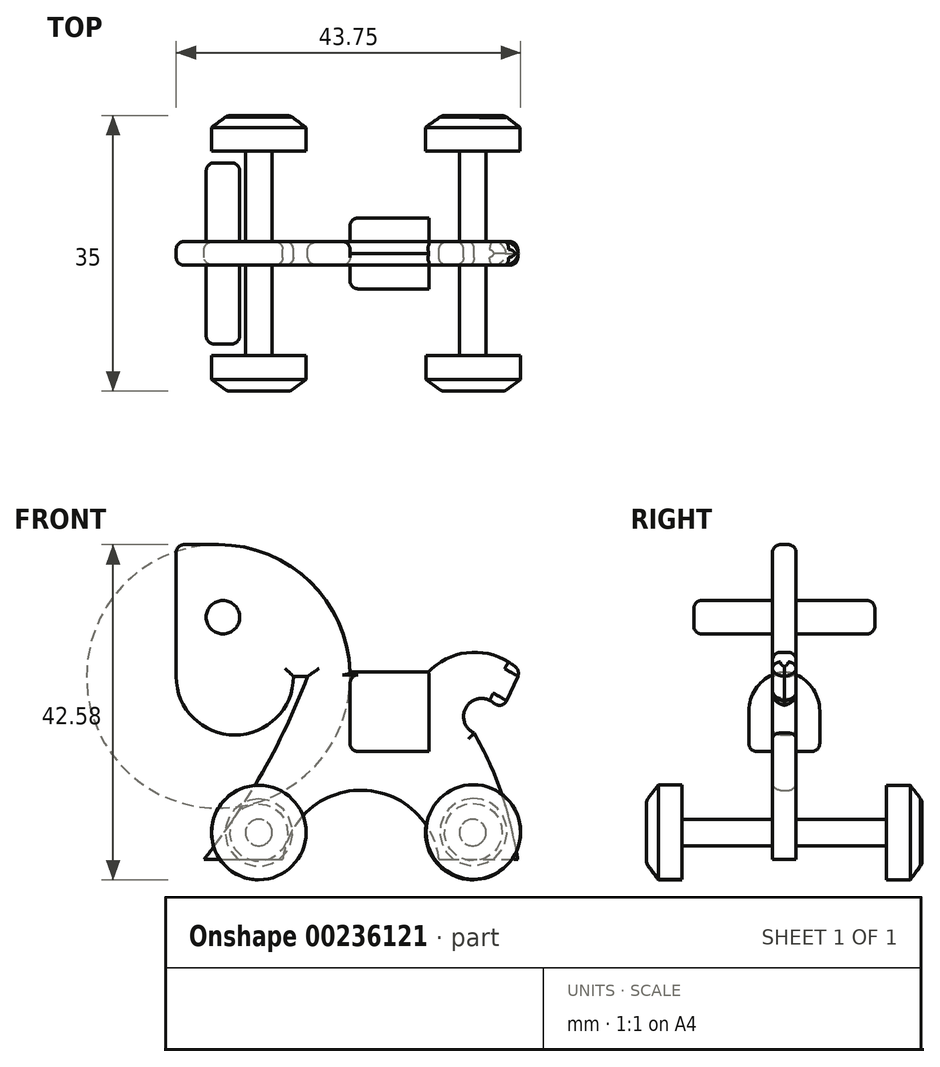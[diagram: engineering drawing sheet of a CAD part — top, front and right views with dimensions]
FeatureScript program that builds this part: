
annotation { "Feature Type Name" : "Feature", "Feature Type Description" : "" }
export const myFeature = defineFeature(function(context is Context, id is Id, definition is map)
    precondition{}
    {
        {
            var Q0;
            Q0=qCreatedBy(makeId("Front.planeOp"),FACE);
            var sketch = newSketch(context, id + "F0", { "sketchPlane" : qUnion([Q0])});
            skLineSegment(sketch, "E0", {"start": v(-55.34, 56.43) * mm, "end": v(-49.98, 56.43) * mm});
            skArc(sketch, "E1", {"start": v(-33.25, 40.31) * mm, "mid": v(-38.36, 51.75) * mm, "end": v(-49.98, 56.43) * mm});
            skLineSegment(sketch, "E2", {"start": v(-33.25, 40.31) * mm, "end": v(-23.25, 40.31) * mm});
            skArc(sketch, "E3", {"start": v(-11.59, 40.31) * mm, "mid": v(-17.42, 42.76) * mm, "end": v(-23.25, 40.31) * mm});
            skLineSegment(sketch, "E4", {"start": v(-55.34, 56.43) * mm, "end": v(-55.34, 39.7) * mm});
            skArc(sketch, "E5", {"start": v(-55.34, 39.7) * mm, "mid": v(-47.9, 32.24) * mm, "end": v(-40.44, 39.7) * mm});
            skLineSegment(sketch, "E6", {"start": v(-40.44, 39.7) * mm, "end": v(-38.64, 39.7) * mm});
            skArc(sketch, "E7", {"start": v(-51.8, 16.43) * mm, "mid": v(-44.34, 27.56) * mm, "end": v(-38.64, 39.7) * mm});
            skLineSegment(sketch, "E8", {"start": v(-51.8, 16.43) * mm, "end": v(-41.8, 16.43) * mm});
            skArc(sketch, "E9", {"start": v(-21.94, 16.43) * mm, "mid": v(-31.87, 25.23) * mm, "end": v(-41.8, 16.43) * mm});
            skArc(sketch, "E10", {"start": v(-14.24, 34.6) * mm, "mid": v(-17.77, 36.53) * mm, "end": v(-17.48, 32.51) * mm});
            skLineSegment(sketch, "E11", {"start": v(-14.24, 34.6) * mm, "end": v(-11.59, 40.31) * mm});
            skArc(sketch, "E12", {"start": v(-11.94, 16.43) * mm, "mid": v(-13.97, 24.73) * mm, "end": v(-17.48, 32.51) * mm});
            skLineSegment(sketch, "E13", {"start": v(-21.94, 16.43) * mm, "end": v(-11.94, 16.43) * mm});
            skCircle(sketch, "E14", {"center": v(-49.4, 47.21) * mm, "radius": 2.13 * mm});
            skCircle(sketch, "E15", {"center": v(-44.84, 19.85) * mm, "radius": 1.7 * mm});
            skCircle(sketch, "E16", {"center": v(-17.67, 19.85) * mm, "radius": 1.7 * mm});
            skSolve(sketch);
        }
        {
            var Q0;
            Q0=qSketchRegion(id+"F0",true);
            extrude(context, id + "F1", {"entities" : qUnion([Q0]), "depth" : 3 * mm});
        }
        {
            var Q0;
            Q0=makeQuery(id+"F1.opExtrude","CAP_FACE",FACE,{"disambiguationData":[OSD([sQuery(id+"F0.wireOp",EDGE,"E0"),sQuery(id+"F0.wireOp",EDGE,"E1"),sQuery(id+"F0.wireOp",EDGE,"E2"),sQuery(id+"F0.wireOp",EDGE,"E3"),sQuery(id+"F0.wireOp",EDGE,"E4"),sQuery(id+"F0.wireOp",EDGE,"E5"),sQuery(id+"F0.wireOp",EDGE,"E6"),sQuery(id+"F0.wireOp",EDGE,"E7"),sQuery(id+"F0.wireOp",EDGE,"E8"),sQuery(id+"F0.wireOp",EDGE,"E9"),sQuery(id+"F0.wireOp",EDGE,"E10"),sQuery(id+"F0.wireOp",EDGE,"E11"),sQuery(id+"F0.wireOp",EDGE,"E12"),sQuery(id+"F0.wireOp",EDGE,"E13"),sQuery(id+"F0.wireOp",EDGE,"E14"),sQuery(id+"F0.wireOp",EDGE,"E15"),sQuery(id+"F0.wireOp",EDGE,"E16")])],"isStart":false});
            var sketch = newSketch(context, id + "F2", { "sketchPlane" : qUnion([Q0])});
            skSolve(sketch);
        }
        {
            var Q0;
            Q0=makeQuery(id+"F2.imprint","IMPRINT",FACE,{"disambiguationData":[TD([[makeQuery(id+"F2.imprint","IMPRINT",EDGE,{"derivedFrom":makeQuery(id+"F1.opExtrude","CAP_EDGE",EDGE,{"disambiguationData":[OSD([sQuery(id+"F0.wireOp",EDGE,"E15")])],"isStart":false})}),1.0]])]});
            var Q1;
            Q1=makeQuery(id+"F2.imprint","IMPRINT",FACE,{"disambiguationData":[TD([[makeQuery(id+"F2.imprint","IMPRINT",EDGE,{"derivedFrom":makeQuery(id+"F1.opExtrude","CAP_EDGE",EDGE,{"disambiguationData":[OSD([sQuery(id+"F0.wireOp",EDGE,"E16")])],"isStart":false})}),1.0]])]});
            extrude(context, id + "F3", {"entities" : qUnion([Q0, Q1]), "operationType" : NewBodyOperationType.ADD, "depth" : 13 * mm, "hasSecondDirection" : true, "secondDirectionOppositeDirection" : true, "secondDirectionDepth" : 16 * mm});
        }
        {
            var Q0;
            Q0=makeQuery(id+"F3.opExtrude","CAP_FACE",FACE,{"disambiguationData":[OSD([sQuery(id+"F0.wireOp",EDGE,"E15")])],"isStart":false});
            var sketch = newSketch(context, id + "F4", { "sketchPlane" : qUnion([Q0])});
            skCircle(sketch, "E17", {"center": v(-44.84, 19.85) * mm, "radius": 6 * mm});
            skCircle(sketch, "E18", {"center": v(-17.59, 19.94) * mm, "radius": 6 * mm});
            skSolve(sketch);
        }
        {
            var Q0;
            Q0=makeQuery(id+"F4.imprint","IMPRINT",FACE,{"disambiguationData":[TD([[makeQuery(id+"F4.imprint","IMPRINT",EDGE,{"derivedFrom":sQuery(id+"F4.wireOp",EDGE,"E18")}),1.0]])]});
            var Q1;
            Q1=makeQuery(id+"F4.imprint","IMPRINT",FACE,{"disambiguationData":[TD([[makeQuery(id+"F4.imprint","IMPRINT",EDGE,{"derivedFrom":sQuery(id+"F4.wireOp",EDGE,"E17")}),1.0]])]});
            var Q2;
            Q2=makeQuery(id+"F4.imprint","IMPRINT",FACE,{"disambiguationData":[TD([[makeQuery(id+"F4.imprint","IMPRINT",EDGE,{"derivedFrom":makeQuery(id+"F3.opExtrude","CAP_EDGE",EDGE,{"disambiguationData":[OSD([sQuery(id+"F0.wireOp",EDGE,"E15")])],"isStart":false})}),1.0]])]});
            extrude(context, id + "F5", {"entities" : qUnion([Q0, Q1, Q2]), "operationType" : NewBodyOperationType.ADD, "endBound" : BoundingType.SYMMETRIC, "oppositeDirection" : true, "depth" : 3 * mm});
        }
        {
            var Q0;
            Q0=makeQuery(id+"F3.opExtrude","CAP_FACE",FACE,{"disambiguationData":[OSD([sQuery(id+"F0.wireOp",EDGE,"E16")])],"isStart":true});
            var sketch = newSketch(context, id + "F6", { "sketchPlane" : qUnion([Q0])});
            skCircle(sketch, "E19", {"center": v(44.85, 19.85) * mm, "radius": 6 * mm});
            skCircle(sketch, "E20", {"center": v(17.67, 19.85) * mm, "radius": 6 * mm});
            skCircle(sketch, "E21", {"center": v(44.85, 19.85) * mm, "radius": 6.02 * mm});
            skSolve(sketch);
        }
        {
            var Q0;
            Q0=makeQuery(id+"F6.imprint","IMPRINT",FACE,{"disambiguationData":[TD([[makeQuery(id+"F6.imprint","IMPRINT",EDGE,{"derivedFrom":sQuery(id+"F6.wireOp",EDGE,"E20")}),1.0]])]});
            var Q1;
            Q1=makeQuery(id+"F6.imprint","IMPRINT",FACE,{"disambiguationData":[TD([[makeQuery(id+"F6.imprint","IMPRINT",EDGE,{"derivedFrom":sQuery(id+"F6.wireOp",EDGE,"E19")}),1.0]])]});
            var Q2;
            Q2=makeQuery(id+"F6.imprint","IMPRINT",FACE,{"disambiguationData":[TD([[makeQuery(id+"F6.imprint","IMPRINT",EDGE,{"derivedFrom":makeQuery(id+"F3.opExtrude","CAP_EDGE",EDGE,{"disambiguationData":[OSD([sQuery(id+"F0.wireOp",EDGE,"E16")])],"isStart":true})}),-1.0]])]});
            extrude(context, id + "F7", {"entities" : qUnion([Q0, Q1, Q2]), "operationType" : NewBodyOperationType.ADD, "endBound" : BoundingType.SYMMETRIC, "oppositeDirection" : true, "depth" : 3 * mm});
        }
        {
            var Q0;
            Q0=makeQuery(id+"F1.opExtrude","CAP_FACE",FACE,{"disambiguationData":[OSD([sQuery(id+"F0.wireOp",EDGE,"E0"),sQuery(id+"F0.wireOp",EDGE,"E1"),sQuery(id+"F0.wireOp",EDGE,"E2"),sQuery(id+"F0.wireOp",EDGE,"E3"),sQuery(id+"F0.wireOp",EDGE,"E4"),sQuery(id+"F0.wireOp",EDGE,"E5"),sQuery(id+"F0.wireOp",EDGE,"E6"),sQuery(id+"F0.wireOp",EDGE,"E7"),sQuery(id+"F0.wireOp",EDGE,"E8"),sQuery(id+"F0.wireOp",EDGE,"E9"),sQuery(id+"F0.wireOp",EDGE,"E10"),sQuery(id+"F0.wireOp",EDGE,"E11"),sQuery(id+"F0.wireOp",EDGE,"E12"),sQuery(id+"F0.wireOp",EDGE,"E13"),sQuery(id+"F0.wireOp",EDGE,"E14"),sQuery(id+"F0.wireOp",EDGE,"E15"),sQuery(id+"F0.wireOp",EDGE,"E16")])],"isStart":true});
            var sketch = newSketch(context, id + "F8", { "sketchPlane" : qUnion([Q0])});
            skLineSegment(sketch, "E22", {"start": v(23.25, 40.31) * mm, "end": v(23.25, 30.15) * mm});
            skLineSegment(sketch, "E23", {"start": v(23.25, 30.15) * mm, "end": v(33.25, 30.15) * mm});
            skLineSegment(sketch, "E24", {"start": v(33.25, 30.15) * mm, "end": v(33.25, 40.31) * mm});
            skLineSegment(sketch, "E25", {"start": v(33.25, 40.31) * mm, "end": v(23.25, 40.31) * mm});
            skSolve(sketch);
        }
        {
            var Q0;
            Q0=makeQuery(id+"F8.imprint","IMPRINT",FACE,{"disambiguationData":[TD([[makeQuery(id+"F8.imprint","IMPRINT",EDGE,{"derivedFrom":sQuery(id+"F8.wireOp",EDGE,"E22")}),1.0]])]});
            extrude(context, id + "F9", {"entities" : qUnion([Q0]), "operationType" : NewBodyOperationType.ADD, "depth" : 3 * mm, "hasSecondDirection" : true, "secondDirectionOppositeDirection" : true, "secondDirectionDepth" : 6 * mm});
        }
        {
            var Q0;
            Q0=makeQuery(id+"F9.opExtrude","CAP_EDGE",EDGE,{"disambiguationData":[OSD([sQuery(id+"F8.wireOp",EDGE,"E25")])],"isStart":false});
            var Q1;
            Q1=makeQuery(id+"F9.opExtrude","CAP_EDGE",EDGE,{"disambiguationData":[OSD([sQuery(id+"F8.wireOp",EDGE,"E25")])],"isStart":true});
            fillet(context, id + "F10", {"entities" : qUnion([Q0, Q1]), "radius" : 5 * mm, "tangentPropagation" : true, "allowEdgeOverflow" : false});
        }
        {
            var Q0;
            Q0=makeQuery(id+"F8.imprint","IMPRINT",FACE,{"disambiguationData":[TD([[makeQuery(id+"F8.imprint","IMPRINT",EDGE,{"derivedFrom":makeQuery(id+"F1.opExtrude","CAP_EDGE",EDGE,{"disambiguationData":[OSD([sQuery(id+"F0.wireOp",EDGE,"E14")])],"isStart":true})}),-1.0]])]});
            extrude(context, id + "F11", {"entities" : qUnion([Q0]), "operationType" : NewBodyOperationType.ADD, "depth" : 10 * mm, "hasSecondDirection" : true, "secondDirectionOppositeDirection" : true, "secondDirectionDepth" : 13 * mm});
        }
        {
            var Q0;
            Q0=makeQuery(id+"F4.imprint","IMPRINT",FACE,{"disambiguationData":[TD([[makeQuery(id+"F4.imprint","IMPRINT",EDGE,{"derivedFrom":sQuery(id+"F4.wireOp",EDGE,"E17")}),1.0]])]});
            var Q1;
            Q1=makeQuery(id+"F4.imprint","IMPRINT",FACE,{"disambiguationData":[TD([[makeQuery(id+"F4.imprint","IMPRINT",EDGE,{"derivedFrom":sQuery(id+"F4.wireOp",EDGE,"E18")}),1.0]])]});
            cPlane(context, id + "F12", {"entities" : qUnion([Q0, Q1]), "cplaneType" : CPlaneType.MID_PLANE, "offset" : 25 * mm, "width" : 150 * mm, "height" : 150 * mm});
        }
        {
            var Q0;
            Q0=qCreatedBy(id+"F12.planeOp",FACE);
            cPlane(context, id + "F13", {"entities" : qUnion([Q0]), "cplaneType" : CPlaneType.OFFSET, "offset" : 3 * mm, "width" : 150 * mm, "height" : 150 * mm});
        }
        {
            var Q0;
            Q0=qCreatedBy(id+"F13.planeOp",FACE);
            var sketch = newSketch(context, id + "F14", { "sketchPlane" : qUnion([Q0])});
            skCircle(sketch, "E26", {"center": v(-44.84, 19.85) * mm, "radius": 4 * mm});
            skCircle(sketch, "E27", {"center": v(-17.59, 19.94) * mm, "radius": 4 * mm});
            skSolve(sketch);
        }
        {
            var Q1;
            Q1=makeQuery(id+"F5.opExtrude","CAP_FACE",FACE,{"disambiguationData":[OSD([sQuery(id+"F4.wireOp",EDGE,"E17")])],"isStart":true});
            var Q2;
            Q2=makeQuery(id+"F14.imprint","IMPRINT",FACE,{"disambiguationData":[TD([[makeQuery(id+"F14.imprint","IMPRINT",EDGE,{"derivedFrom":sQuery(id+"F14.wireOp",EDGE,"E26")}),1.0]])]});
            loft(context, id + "F15", {"operationType" : NewBodyOperationType.ADD, "sheetProfilesArray" : [{ "sheetProfileEntities" : qUnion([Q1]) }, { "sheetProfileEntities" : qUnion([Q2]) }]});
        }
        {
            var Q0;
            Q0=qCreatedBy(id+"F13.planeOp",FACE);
            var sketch = newSketch(context, id + "F16", { "sketchPlane" : qUnion([Q0])});
            skCircle(sketch, "E28", {"center": v(-17.59, 19.94) * mm, "radius": 4 * mm});
            skSolve(sketch);
        }
        {
            var Q1;
            Q1=makeQuery(id+"F5.opExtrude","CAP_FACE",FACE,{"disambiguationData":[OSD([sQuery(id+"F4.wireOp",EDGE,"E18")])],"isStart":true});
            var Q2;
            Q2=makeQuery(id+"F16.imprint","IMPRINT",FACE,{"disambiguationData":[TD([[makeQuery(id+"F16.imprint","IMPRINT",EDGE,{"derivedFrom":sQuery(id+"F16.wireOp",EDGE,"E28")}),1.0]])]});
            loft(context, id + "F17", {"operationType" : NewBodyOperationType.ADD, "sheetProfilesArray" : [{ "sheetProfileEntities" : qUnion([Q1]) }, { "sheetProfileEntities" : qUnion([Q2]) }]});
        }
        {
            var Q0;
            Q0=makeQuery(id+"F7.opExtrude","CAP_FACE",FACE,{"disambiguationData":[OSD([sQuery(id+"F6.wireOp",EDGE,"E20")])],"isStart":true});
            var sketch = newSketch(context, id + "F18", { "sketchPlane" : qUnion([Q0])});
            skSolve(sketch);
        }
        {
            var Q0;
            Q0=makeQuery(id+"F18.imprint","IMPRINT",FACE,{"disambiguationData":[TD([[makeQuery(id+"F18.imprint","IMPRINT",EDGE,{"derivedFrom":makeQuery(id+"F7.opExtrude","CAP_EDGE",EDGE,{"disambiguationData":[OSD([sQuery(id+"F6.wireOp",EDGE,"E20")])],"isStart":true})}),1.0]])]});
            var Q1;
            Q1=makeQuery(id+"F7.opExtrude","CAP_FACE",FACE,{"disambiguationData":[OSD([sQuery(id+"F6.wireOp",EDGE,"E19")])],"isStart":true});
            cPlane(context, id + "F19", {"entities" : qUnion([Q0, Q1]), "cplaneType" : CPlaneType.MID_PLANE, "offset" : 25 * mm, "width" : 150 * mm, "height" : 150 * mm});
        }
        {
            var Q0;
            Q0=qCreatedBy(id+"F19.planeOp",FACE);
            cPlane(context, id + "F20", {"entities" : qUnion([Q0]), "cplaneType" : CPlaneType.OFFSET, "offset" : 1.5 * mm, "width" : 150 * mm, "height" : 150 * mm});
        }
        {
            var Q0;
            Q0=qCreatedBy(id+"F20.planeOp",FACE);
            var sketch = newSketch(context, id + "F21", { "sketchPlane" : qUnion([Q0])});
            skCircle(sketch, "E29", {"center": v(44.84, 19.85) * mm, "radius": 4 * mm});
            skSolve(sketch);
        }
        {
            var Q0;
            Q0=makeQuery(id+"F7.opExtrude","CAP_FACE",FACE,{"disambiguationData":[OSD([sQuery(id+"F6.wireOp",EDGE,"E19")])],"isStart":true});
            var Q1;
            Q1=makeQuery(id+"F21.imprint","IMPRINT",FACE,{"disambiguationData":[TD([[makeQuery(id+"F21.imprint","IMPRINT",EDGE,{"derivedFrom":sQuery(id+"F21.wireOp",EDGE,"E29")}),1.0]])]});
            loft(context, id + "F22", {"sheetProfilesArray" : [{ "sheetProfileEntities" : qUnion([Q0]) }, { "sheetProfileEntities" : qUnion([Q1]) }]});
        }
        {
            var Q0;
            Q0=qCreatedBy(id+"F20.planeOp",FACE);
            var sketch = newSketch(context, id + "F23", { "sketchPlane" : qUnion([Q0])});
            skCircle(sketch, "E30", {"center": v(17.59, 19.94) * mm, "radius": 4 * mm});
            skSolve(sketch);
        }
        {
            var Q0;
            Q0=makeQuery(id+"F18.imprint","IMPRINT",FACE,{"disambiguationData":[TD([[makeQuery(id+"F18.imprint","IMPRINT",EDGE,{"derivedFrom":makeQuery(id+"F7.opExtrude","CAP_EDGE",EDGE,{"disambiguationData":[OSD([sQuery(id+"F6.wireOp",EDGE,"E20")])],"isStart":true})}),1.0]])]});
            var Q1;
            Q1=makeQuery(id+"F23.imprint","IMPRINT",FACE,{"disambiguationData":[TD([[makeQuery(id+"F23.imprint","IMPRINT",EDGE,{"derivedFrom":sQuery(id+"F23.wireOp",EDGE,"E30")}),1.0]])]});
            loft(context, id + "F24", {"sheetProfilesArray" : [{ "sheetProfileEntities" : qUnion([Q0]) }, { "sheetProfileEntities" : qUnion([Q1]) }]});
        }
        {
            var Q0;
            Q0=makeQuery(id+"F1.opExtrude","CAP_EDGE",EDGE,{"disambiguationData":[OSD([sQuery(id+"F0.wireOp",EDGE,"E0")])],"isStart":false});
            var Q1;
            Q1=makeQuery(id+"F1.opExtrude","CAP_EDGE",EDGE,{"disambiguationData":[OSD([sQuery(id+"F0.wireOp",EDGE,"E1")])],"isStart":true});
            fillet(context, id + "F25", {"entities" : qUnion([Q0, Q1]), "radius" : 1 * mm, "tangentPropagation" : true, "allowEdgeOverflow" : false});
        }
        {
            var Q0;
            Q0=makeQuery(id+"F1.opExtrude","CAP_EDGE",EDGE,{"disambiguationData":[OSD([sQuery(id+"F0.wireOp",EDGE,"E11")])],"isStart":true});
            var Q1;
            Q1=makeQuery(id+"F1.opExtrude","CAP_EDGE",EDGE,{"disambiguationData":[OSD([sQuery(id+"F0.wireOp",EDGE,"E11")])],"isStart":false});
            fillet(context, id + "F26", {"entities" : qUnion([Q0, Q1]), "radius" : 2 * mm, "tangentPropagation" : true, "allowEdgeOverflow" : false});
        }
        {
            var Q0;
            Q0=makeQuery(id+"F11.opExtrude","CAP_EDGE",EDGE,{"disambiguationData":[OSD([sQuery(id+"F0.wireOp",EDGE,"E14")])],"isStart":false});
            var Q1;
            Q1=makeQuery(id+"F11.opExtrude","CAP_EDGE",EDGE,{"disambiguationData":[OSD([sQuery(id+"F0.wireOp",EDGE,"E14")])],"isStart":true});
            var Q2;
            Q2=makeQuery(id+"F1.opExtrude","CAP_EDGE",EDGE,{"disambiguationData":[OSD([sQuery(id+"F0.wireOp",EDGE,"E3")])],"isStart":true});
            var Q3;
            Q3=makeQuery(id+"F1.opExtrude","CAP_EDGE",EDGE,{"disambiguationData":[OSD([sQuery(id+"F0.wireOp",EDGE,"E3")])],"isStart":false});
            fillet(context, id + "F27", {"entities" : qUnion([Q0, Q1, Q2, Q3]), "radius" : 1 * mm, "tangentPropagation" : true, "allowEdgeOverflow" : false});
        }
        {
            var Q0;
            Q0=makeQuery(id+"F9.opExtrude","CAP_EDGE",EDGE,{"disambiguationData":[OSD([sQuery(id+"F8.wireOp",EDGE,"E23")])],"isStart":true});
            var Q1;
            Q1=makeQuery(id+"F9.opExtrude","CAP_EDGE",EDGE,{"disambiguationData":[OSD([sQuery(id+"F8.wireOp",EDGE,"E23")])],"isStart":false});
            fillet(context, id + "F28", {"entities" : qUnion([Q0, Q1]), "radius" : 1 * mm, "tangentPropagation" : true, "allowEdgeOverflow" : false});
        }
        {
            var Q0;
            Q0=makeQuery(id+"F15.opLoft","MID_CAP_EDGE",EDGE,{"disambiguationData":[OSD([sQuery(id+"F4.wireOp",EDGE,"E17"),sQuery(id+"F14.wireOp",EDGE,"E26")])],"capPos":1.0});
            var Q1;
            Q1=makeQuery(id+"F17.opLoft","MID_CAP_EDGE",EDGE,{"disambiguationData":[OSD([sQuery(id+"F4.wireOp",EDGE,"E18"),sQuery(id+"F16.wireOp",EDGE,"E28")])],"capPos":1.0});
            var Q2;
            Q2=makeQuery(id+"F24.opLoft","MID_CAP_EDGE",EDGE,{"disambiguationData":[OSD([sQuery(id+"F6.wireOp",EDGE,"E20"),sQuery(id+"F23.wireOp",EDGE,"E30")])],"capPos":1.0});
            var Q3;
            Q3=makeQuery(id+"F22.opLoft","MID_CAP_EDGE",EDGE,{"disambiguationData":[OSD([sQuery(id+"F6.wireOp",EDGE,"E19"),sQuery(id+"F21.wireOp",EDGE,"E29")])],"capPos":1.0});
            var Q4;
            Q4=makeQuery(id+"F1.opExtrude","CAP_EDGE",EDGE,{"disambiguationData":[OSD([sQuery(id+"F0.wireOp",EDGE,"E4")])],"isStart":true});
            var Q5;
            Q5=makeQuery(id+"F1.opExtrude","CAP_EDGE",EDGE,{"disambiguationData":[OSD([sQuery(id+"F0.wireOp",EDGE,"E10")])],"isStart":true});
            var Q6;
            Q6=makeQuery(id+"F1.opExtrude","CAP_EDGE",EDGE,{"disambiguationData":[OSD([sQuery(id+"F0.wireOp",EDGE,"E10")])],"isStart":false});
            var Q7;
            Q7=makeQuery(id+"F1.opExtrude","CAP_EDGE",EDGE,{"disambiguationData":[OSD([sQuery(id+"F0.wireOp",EDGE,"E12")])],"isStart":false});
            var Q8;
            Q8=makeQuery(id+"F1.opExtrude","CAP_EDGE",EDGE,{"disambiguationData":[OSD([sQuery(id+"F0.wireOp",EDGE,"E12")])],"isStart":true});
            fillet(context, id + "F29", {"entities" : qUnion([Q0, Q1, Q2, Q3, Q4, Q5, Q6, Q7, Q8]), "radius" : 1 * mm, "tangentPropagation" : true, "allowEdgeOverflow" : false});
        }
        {
            var Q0;
            Q0=makeQuery(id+"F1.opExtrude","CAP_EDGE",EDGE,{"disambiguationData":[OSD([sQuery(id+"F0.wireOp",EDGE,"E6")])],"isStart":false});
            var Q1;
            Q1=makeQuery(id+"F1.opExtrude","CAP_EDGE",EDGE,{"disambiguationData":[OSD([sQuery(id+"F0.wireOp",EDGE,"E7")])],"isStart":false});
            var Q2;
            Q2=makeQuery(id+"F1.opExtrude","CAP_EDGE",EDGE,{"disambiguationData":[OSD([sQuery(id+"F0.wireOp",EDGE,"E6")])],"isStart":true});
            var Q3;
            Q3=makeQuery(id+"F1.opExtrude","CAP_EDGE",EDGE,{"disambiguationData":[OSD([sQuery(id+"F0.wireOp",EDGE,"E7")])],"isStart":true});
            var Q4;
            Q4=makeQuery(id+"F1.opExtrude","CAP_EDGE",EDGE,{"disambiguationData":[OSD([sQuery(id+"F0.wireOp",EDGE,"E9")])],"isStart":false});
            var Q5;
            Q5=makeQuery(id+"F1.opExtrude","CAP_EDGE",EDGE,{"disambiguationData":[OSD([sQuery(id+"F0.wireOp",EDGE,"E9")])],"isStart":true});
            fillet(context, id + "F30", {"entities" : qUnion([Q0, Q1, Q2, Q3, Q4, Q5]), "radius" : 1 * mm, "tangentPropagation" : true, "allowEdgeOverflow" : false});
        }
        {
            var Q0;
            {var subQ1=sQuery(id+"F8.wireOp",EDGE,"E25");var subQ2=sQuery(id+"F8.wireOp",EDGE,"E24");var subQ3=sQuery(id+"F8.wireOp",EDGE,"E23");Q0=makeQuery(id+"F10.opFillet","BLEND_EDGE",EDGE,{"blendedFrom":[makeQuery(id+"F9.opExtrude","CAP_EDGE",EDGE,{"disambiguationData":[OSD([subQ1])],"isStart":false}),makeQuery(id+"F9.boolean.opBoolean","SPLIT",FACE,{"disambiguationData":[TD([makeQuery(id+"F9.opExtrude","CAP_FACE",FACE,{"disambiguationData":[OSD([sQuery(id+"F8.wireOp",EDGE,"E22"),subQ3,subQ2,subQ1])],"isStart":false})])],"derivedFrom":makeQuery(id+"F9.opExtrude","SWEPT_FACE",FACE,{"disambiguationData":[OSD([subQ2])]})})],"blendedInto":[makeQuery(id+"F9.boolean.opBoolean","SPLIT",FACE,{"disambiguationData":[TD([makeQuery(id+"F9.opExtrude","CAP_FACE",FACE,{"disambiguationData":[OSD([sQuery(id+"F8.wireOp",EDGE,"E22"),subQ3,subQ2,subQ1])],"isStart":false})])],"derivedFrom":makeQuery(id+"F9.opExtrude","SWEPT_FACE",FACE,{"disambiguationData":[OSD([subQ2])]})})]});}
            var Q1;
            {var subQ1=sQuery(id+"F8.wireOp",EDGE,"E25");var subQ2=sQuery(id+"F8.wireOp",EDGE,"E24");var subQ3=sQuery(id+"F8.wireOp",EDGE,"E23");Q1=makeQuery(id+"F10.opFillet","BLEND_EDGE",EDGE,{"blendedFrom":[makeQuery(id+"F9.opExtrude","CAP_EDGE",EDGE,{"disambiguationData":[OSD([subQ1])],"isStart":true}),makeQuery(id+"F9.boolean.opBoolean","SPLIT",FACE,{"disambiguationData":[TD([makeQuery(id+"F9.opExtrude","CAP_FACE",FACE,{"disambiguationData":[OSD([sQuery(id+"F8.wireOp",EDGE,"E22"),subQ3,subQ2,subQ1])],"isStart":true})])],"derivedFrom":makeQuery(id+"F9.opExtrude","SWEPT_FACE",FACE,{"disambiguationData":[OSD([subQ2])]})})],"blendedInto":[makeQuery(id+"F9.boolean.opBoolean","SPLIT",FACE,{"disambiguationData":[TD([makeQuery(id+"F9.opExtrude","CAP_FACE",FACE,{"disambiguationData":[OSD([sQuery(id+"F8.wireOp",EDGE,"E22"),subQ3,subQ2,subQ1])],"isStart":true})])],"derivedFrom":makeQuery(id+"F9.opExtrude","SWEPT_FACE",FACE,{"disambiguationData":[OSD([subQ2])]})})]});}
            fillet(context, id + "F31", {"entities" : qUnion([Q0, Q1]), "radius" : 1 * mm, "tangentPropagation" : true, "allowEdgeOverflow" : false});
        }
    });
